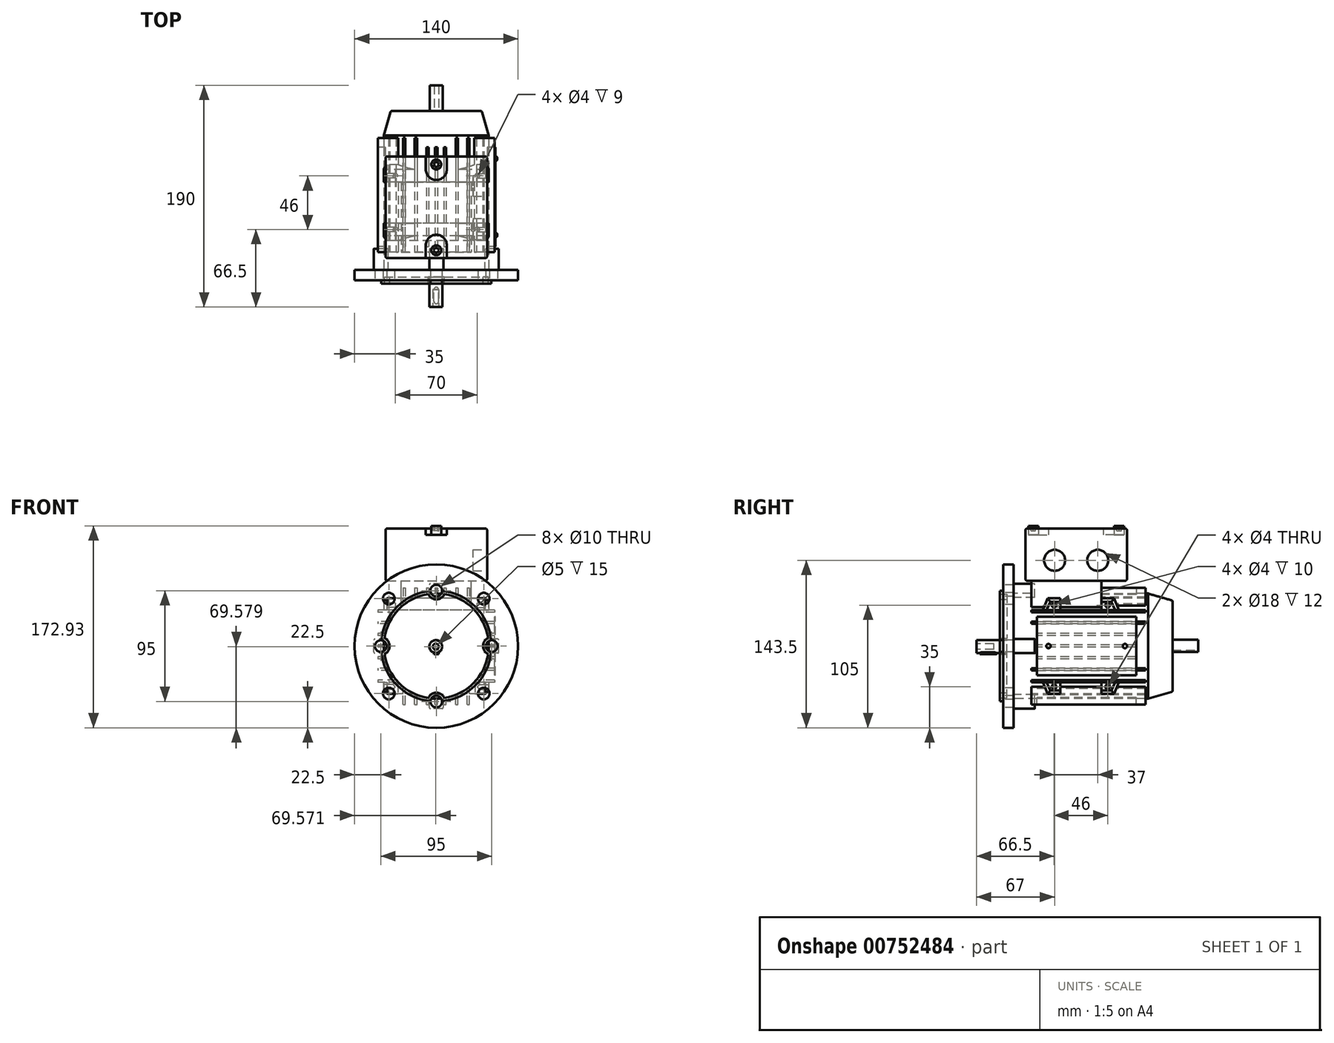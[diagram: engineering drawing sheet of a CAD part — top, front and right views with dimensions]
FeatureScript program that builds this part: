
annotation { "Feature Type Name" : "Feature", "Feature Type Description" : "" }
export const myFeature = defineFeature(function(context is Context, id is Id, definition is map)
    precondition{}
    {
        {
            var Q0;
            Q0=qCreatedBy(makeId("Front.planeOp"),FACE);
            var sketch = newSketch(context, id + "F0", { "sketchPlane" : qUnion([Q0])});
            skCircle(sketch, "E0", {"center": v(0, 0) * mm, "radius": 70 * mm});
            skSolve(sketch);
        }
        {
            var Q0;
            Q0 = qSketchRegion(id + "F0", true);
            extrude(context, id + "F1", {"entities" : qUnion([Q0]), "oppositeDirection" : true, "depth" : 9 * mm, "offsetDistance" : 25.4 * mm});
        }
        {
            var Q0;
            Q0=makeQuery(id+"F1.opExtrude","CAP_FACE",FACE,{"disambiguationData":[OSD([sQuery(id+"F0.wireOp",EDGE,"E0")])],"isStart":true});
            var sketch = newSketch(context, id + "F2", { "sketchPlane" : qUnion([Q0])});
            skCircle(sketch, "E1", {"center": v(-40.66, 40.66) * mm, "radius": 5 * mm});
            skCircle(sketch, "E2", {"center": v(-40.66, -40.66) * mm, "radius": 5 * mm});
            skCircle(sketch, "E3", {"center": v(40.66, -40.66) * mm, "radius": 5 * mm});
            skCircle(sketch, "E4", {"center": v(40.66, 40.66) * mm, "radius": 5 * mm});
            skCircle(sketch, "E5", {"center": v(0, 0) * mm, "radius": 57.5 * mm, "construction": true});
            skLineSegment(sketch, "E6", {"start": v(-40.66, -40.66) * mm, "end": v(40.66, 40.66) * mm, "construction": true});
            skLineSegment(sketch, "E7", {"start": v(-40.66, 40.66) * mm, "end": v(40.66, -40.66) * mm, "construction": true});
            skLineSegment(sketch, "E8", {"start": v(-57.5, 0) * mm, "end": v(57.5, 0) * mm, "construction": true});
            skSolve(sketch);
        }
        {
            var Q0;
            Q0 = qSketchRegion(id + "F2", true);
            extrude(context, id + "F3", {"entities" : qUnion([Q0]), "operationType" : NewBodyOperationType.REMOVE, "endBound" : BoundingType.UP_TO_NEXT, "oppositeDirection" : true, "depth" : 25.4 * mm, "offsetDistance" : 25.4 * mm});
        }
        {
            var Q0;
            Q0=makeQuery(id+"F1.opExtrude","CAP_FACE",FACE,{"disambiguationData":[OSD([sQuery(id+"F0.wireOp",EDGE,"E0")])],"isStart":true});
            var sketch = newSketch(context, id + "F4", { "sketchPlane" : qUnion([Q0])});
            skCircle(sketch, "E9", {"center": v(0, 0) * mm, "radius": 47.5 * mm, "construction": true});
            skCircle(sketch, "E10", {"center": v(0, 47.5) * mm, "radius": 5 * mm});
            skCircle(sketch, "E11", {"center": v(47.5, 0) * mm, "radius": 5 * mm});
            skCircle(sketch, "E12", {"center": v(0, -47.5) * mm, "radius": 5 * mm});
            skCircle(sketch, "E13", {"center": v(-47.5, 0) * mm, "radius": 5 * mm});
            skSolve(sketch);
        }
        {
            var Q0;
            Q0 = qSketchRegion(id + "F4", true);
            extrude(context, id + "F5", {"entities" : qUnion([Q0]), "operationType" : NewBodyOperationType.REMOVE, "endBound" : BoundingType.THROUGH_ALL, "oppositeDirection" : true, "depth" : 8 * mm, "offsetDistance" : 25 * mm});
        }
        {
            var Q0;
            Q0=qCreatedBy(makeId("Front.planeOp"),FACE);
            var sketch = newSketch(context, id + "F6", { "sketchPlane" : qUnion([Q0])});
            skArc(sketch, "E14", {"start": v(-5, 47.24) * mm, "mid": v(-33.59, 33.59) * mm, "end": v(-47.24, 5) * mm});
            skArc(sketch, "E15", {"start": v(-5, 47.24) * mm, "mid": v(0, 42.5) * mm, "end": v(5, 47.24) * mm});
            skArc(sketch, "E16", {"start": v(47.24, 5) * mm, "mid": v(42.5, 0) * mm, "end": v(47.24, -5) * mm});
            skArc(sketch, "E17", {"start": v(5, -47.24) * mm, "mid": v(0, -42.5) * mm, "end": v(-5, -47.24) * mm});
            skArc(sketch, "E18", {"start": v(-47.24, -5) * mm, "mid": v(-42.5, 0) * mm, "end": v(-47.24, 5) * mm});
            skArc(sketch, "E19.trimOffspring", {"start": v(47.24, 5) * mm, "mid": v(33.59, 33.59) * mm, "end": v(5, 47.24) * mm});
            skArc(sketch, "E20.trimOffspring", {"start": v(5, -47.24) * mm, "mid": v(33.59, -33.59) * mm, "end": v(47.24, -5) * mm});
            skArc(sketch, "E21.trimOffspring", {"start": v(-47.24, -5) * mm, "mid": v(-33.59, -33.59) * mm, "end": v(-5, -47.24) * mm});
            skArc(sketch, "E22.0", {"start": v(6.86, -44.47) * mm, "mid": v(31.82, -31.82) * mm, "end": v(44.47, -6.86) * mm});
            skArc(sketch, "E22.1", {"start": v(44.47, 6.86) * mm, "mid": v(40, 0) * mm, "end": v(44.47, -6.86) * mm});
            skArc(sketch, "E22.2", {"start": v(6.86, -44.47) * mm, "mid": v(0, -40) * mm, "end": v(-6.86, -44.47) * mm});
            skArc(sketch, "E22.3", {"start": v(44.47, 6.86) * mm, "mid": v(31.82, 31.82) * mm, "end": v(6.86, 44.47) * mm});
            skArc(sketch, "E22.4", {"start": v(-44.47, -6.86) * mm, "mid": v(-31.82, -31.82) * mm, "end": v(-6.86, -44.47) * mm});
            skArc(sketch, "E22.5", {"start": v(-44.47, -6.86) * mm, "mid": v(-40, 0) * mm, "end": v(-44.47, 6.86) * mm});
            skArc(sketch, "E22.6", {"start": v(-6.86, 44.47) * mm, "mid": v(-31.82, 31.82) * mm, "end": v(-44.47, 6.86) * mm});
            skArc(sketch, "E22.7", {"start": v(-6.86, 44.47) * mm, "mid": v(0, 40) * mm, "end": v(6.86, 44.47) * mm});
            skSolve(sketch);
        }
        {
            var Q0;
            Q0=makeQuery(id+"F6.imprint","IMPRINT",FACE,{"disambiguationData":[TD([[makeQuery(id+"F6.imprint","IMPRINT",EDGE,{"derivedFrom":sQuery(id+"F6.wireOp",EDGE,"E14")}),1.0]])]});
            extrude(context, id + "F7", {"entities" : qUnion([Q0]), "operationType" : NewBodyOperationType.ADD, "depth" : 3 * mm, "offsetDistance" : 25 * mm});
        }
        {
            var Q0;
            Q0=makeQuery(id+"F4.imprint","IMPRINT",FACE,{"disambiguationData":[TD([[makeQuery(id+"F4.imprint","IMPRINT",EDGE,{"derivedFrom":sQuery(id+"F4.wireOp",EDGE,"E10")}),-1.0]])]});
            var sketch = newSketch(context, id + "F8", { "sketchPlane" : qUnion([Q0])});
            skArc(sketch, "E23.0", {"start": v(-6.86, 44.47) * mm, "mid": v(-31.82, 31.82) * mm, "end": v(-44.47, 6.86) * mm});
            skArc(sketch, "E24.0", {"start": v(-6.86, 44.47) * mm, "mid": v(0, 40) * mm, "end": v(6.86, 44.47) * mm});
            skArc(sketch, "E25.0", {"start": v(44.47, 6.86) * mm, "mid": v(31.82, 31.82) * mm, "end": v(6.86, 44.47) * mm});
            skArc(sketch, "E26.0", {"start": v(-44.47, -6.86) * mm, "mid": v(-40, 0) * mm, "end": v(-44.47, 6.86) * mm});
            skArc(sketch, "E27.0", {"start": v(-44.47, -6.86) * mm, "mid": v(-31.82, -31.82) * mm, "end": v(-6.86, -44.47) * mm});
            skArc(sketch, "E28.0", {"start": v(6.86, -44.47) * mm, "mid": v(0, -40) * mm, "end": v(-6.86, -44.47) * mm});
            skArc(sketch, "E29.0", {"start": v(6.86, -44.47) * mm, "mid": v(31.82, -31.82) * mm, "end": v(44.47, -6.86) * mm});
            skArc(sketch, "E30.0", {"start": v(44.47, 6.86) * mm, "mid": v(40, 0) * mm, "end": v(44.47, -6.86) * mm});
            skSolve(sketch);
        }
        {
            var Q0;
            Q0 = qSketchRegion(id + "F8", true);
            extrude(context, id + "F9", {"entities" : qUnion([Q0]), "operationType" : NewBodyOperationType.REMOVE, "oppositeDirection" : true, "depth" : 3 * mm, "offsetDistance" : 25 * mm});
        }
        {
            var Q0;
            Q0=makeQuery(id+"F4.imprint","IMPRINT",FACE,{"disambiguationData":[TD([[makeQuery(id+"F4.imprint","IMPRINT",EDGE,{"derivedFrom":sQuery(id+"F4.wireOp",EDGE,"E10")}),-1.0]])]});
            var sketch = newSketch(context, id + "F10", { "sketchPlane" : qUnion([Q0])});
            skCircle(sketch, "E31", {"center": v(-0.43, -0.42) * mm, "radius": 5.5 * mm});
            skSolve(sketch);
        }
        {
            var Q0;
            Q0 = qSketchRegion(id + "F10", true);
            var Q1;
            Q1=makeQuery(id+"F9.boolean.opBoolean","COPY",FACE,{"derivedFrom":makeQuery(id+"F9.opExtrude","CAP_FACE",FACE,{"disambiguationData":[OSD([sQuery(id+"F8.wireOp",EDGE,"E23.0"),sQuery(id+"F8.wireOp",EDGE,"E24.0"),sQuery(id+"F8.wireOp",EDGE,"E25.0"),sQuery(id+"F8.wireOp",EDGE,"E26.0"),sQuery(id+"F8.wireOp",EDGE,"E27.0"),sQuery(id+"F8.wireOp",EDGE,"E28.0"),sQuery(id+"F8.wireOp",EDGE,"E29.0"),sQuery(id+"F8.wireOp",EDGE,"E30.0")])],"isStart":false})});
            extrude(context, id + "F11", {"entities" : qUnion([Q0]), "depth" : 23 * mm, "offsetDistance" : 25 * mm, "hasSecondDirection" : true, "secondDirectionBound" : SecondDirectionBoundingType.UP_TO_SURFACE, "secondDirectionOppositeDirection" : true, "secondDirectionDepth" : 25 * mm, "secondDirectionBoundEntityFace" : qUnion([Q1])});
        }
        {
            var Q0;
            Q0=qCreatedBy(makeId("Front.planeOp"),FACE);
            cPlane(context, id + "F12", {"entities" : qUnion([Q0]), "cplaneType" : CPlaneType.OFFSET, "offset" : 124 * mm, "oppositeDirection" : true, "width" : 150 * mm, "height" : 150 * mm});
        }
        {
            var Q0;
            Q0=qCreatedBy(id+"F12.planeOp",FACE);
            var sketch = newSketch(context, id + "F13", { "sketchPlane" : qUnion([Q0])});
            skPoint(sketch, "E32.middle", {"position": v(0, 0) * mm});
            skCircle(sketch, "E33", {"center": v(0, 0) * mm, "radius": 56 * mm});
            skSolve(sketch);
        }
        {
            var Q0;
            Q0=makeQuery(id+"F1.opExtrude","CAP_FACE",FACE,{"disambiguationData":[OSD([sQuery(id+"F0.wireOp",EDGE,"E0")])],"isStart":false});
            var sketch = newSketch(context, id + "F14", { "sketchPlane" : qUnion([Q0])});
            skCircle(sketch, "E34", {"center": v(0, 0) * mm, "radius": 45 * mm});
            skSolve(sketch);
        }
        {
            var Q0;
            Q0 = qSketchRegion(id + "F14", true);
            var Q1;
            Q1=makeQuery(id+"Fn6rnlRLXiBt8Ug_1.opExtrude","CAP_FACE",FACE,{"disambiguationData":[OSD([sQuery(id+"F13.wireOp",EDGE,"E33")])],"isStart":true});
            extrude(context, id + "F15", {"entities" : qUnion([Q0]), "depth" : 115 * mm, "endBoundEntityFace" : qUnion([Q1]), "offsetDistance" : 25 * mm});
        }
        {
            var Q0;
            Q0=qCreatedBy(makeId("Right.planeOp"),FACE);
            var sketch = newSketch(context, id + "F16", { "sketchPlane" : qUnion([Q0])});
            skLineSegment(sketch, "E35.bottom", {"start": v(24, 21) * mm, "end": v(122, 21) * mm});
            skLineSegment(sketch, "E35.top", {"start": v(24, 19) * mm, "end": v(122, 19) * mm});
            skLineSegment(sketch, "E35.left", {"start": v(24, 21) * mm, "end": v(24, 19) * mm});
            skLineSegment(sketch, "E35.right", {"start": v(122, 21) * mm, "end": v(122, 19) * mm});
            skLineSegment(sketch, "E36.bottom", {"start": v(29, 11) * mm, "end": v(114, 11) * mm});
            skLineSegment(sketch, "E36.top", {"start": v(29, 9) * mm, "end": v(114, 9) * mm});
            skLineSegment(sketch, "E36.left", {"start": v(29, 11) * mm, "end": v(29, 9) * mm});
            skLineSegment(sketch, "E36.right", {"start": v(114, 11) * mm, "end": v(114, 9) * mm});
            skLineSegment(sketch, "E37.bottom", {"start": v(29, 1) * mm, "end": v(114, 1) * mm});
            skLineSegment(sketch, "E37.top", {"start": v(29, -1) * mm, "end": v(114, -1) * mm});
            skLineSegment(sketch, "E37.left", {"start": v(29, 1) * mm, "end": v(29, -1) * mm});
            skLineSegment(sketch, "E37.right", {"start": v(114, 1) * mm, "end": v(114, -1) * mm});
            skLineSegment(sketch, "E38.bottom", {"start": v(24, 31) * mm, "end": v(122, 31) * mm});
            skLineSegment(sketch, "E38.top", {"start": v(24, 29) * mm, "end": v(122, 29) * mm});
            skLineSegment(sketch, "E38.left", {"start": v(24, 31) * mm, "end": v(24, 29) * mm});
            skLineSegment(sketch, "E38.right", {"start": v(122, 31) * mm, "end": v(122, 29) * mm});
            skLineSegment(sketch, "E39.bottom", {"start": v(29, -9) * mm, "end": v(114, -9) * mm});
            skLineSegment(sketch, "E39.top", {"start": v(29, -11) * mm, "end": v(114, -11) * mm});
            skLineSegment(sketch, "E39.left", {"start": v(29, -9) * mm, "end": v(29, -11) * mm});
            skLineSegment(sketch, "E39.right", {"start": v(114, -9) * mm, "end": v(114, -11) * mm});
            skLineSegment(sketch, "E40.bottom", {"start": v(24, -19) * mm, "end": v(122, -19) * mm});
            skLineSegment(sketch, "E40.top", {"start": v(24, -21) * mm, "end": v(122, -21) * mm});
            skLineSegment(sketch, "E40.left", {"start": v(24, -19) * mm, "end": v(24, -21) * mm});
            skLineSegment(sketch, "E40.right", {"start": v(122, -19) * mm, "end": v(122, -21) * mm});
            skLineSegment(sketch, "E41.bottom", {"start": v(24, -29) * mm, "end": v(122, -29) * mm});
            skLineSegment(sketch, "E41.top", {"start": v(24, -31) * mm, "end": v(122, -31) * mm});
            skLineSegment(sketch, "E41.left", {"start": v(24, -29) * mm, "end": v(24, -31) * mm});
            skLineSegment(sketch, "E41.right", {"start": v(122, -29) * mm, "end": v(122, -31) * mm});
            skLineSegment(sketch, "E42", {"start": v(0, 0) * mm, "end": v(29, 0) * mm, "construction": true});
            skLineSegment(sketch, "E43", {"start": v(122, 29) * mm, "end": v(122, -29) * mm, "construction": true});
            skLineSegment(sketch, "E44", {"start": v(114, 9) * mm, "end": v(114, -9) * mm, "construction": true});
            skSolve(sketch);
        }
        {
            var Q0;
            Q0 = qSketchRegion(id + "F16", true);
            extrude(context, id + "F17", {"entities" : qUnion([Q0]), "operationType" : NewBodyOperationType.ADD, "endBound" : BoundingType.SYMMETRIC, "depth" : 100 * mm, "offsetDistance" : 25 * mm});
        }
        {
            var Q0;
            Q0=qCreatedBy(makeId("Top.planeOp"),FACE);
            cPlane(context, id + "F18", {"entities" : qUnion([Q0]), "cplaneType" : CPlaneType.OFFSET, "offset" : 56 * mm, "width" : 150 * mm, "height" : 150 * mm});
        }
        {
            var Q0;
            Q0=qCreatedBy(id+"F18.planeOp",FACE);
            var sketch = newSketch(context, id + "F19", { "sketchPlane" : qUnion([Q0])});
            skLineSegment(sketch, "E45.bottom", {"start": v(-43.5, 19) * mm, "end": v(43.5, 19) * mm});
            skLineSegment(sketch, "E45.top", {"start": v(-43.5, 106) * mm, "end": v(43.5, 106) * mm});
            skLineSegment(sketch, "E45.left", {"start": v(-43.5, 19) * mm, "end": v(-43.5, 106) * mm});
            skLineSegment(sketch, "E45.right", {"start": v(43.5, 19) * mm, "end": v(43.5, 106) * mm});
            skSolve(sketch);
        }
        {
            var Q0;
            Q0 = qSketchRegion(id + "F19", true);
            extrude(context, id + "F20", {"entities" : qUnion([Q0]), "depth" : 44.68 * mm, "offsetDistance" : 25 * mm});
        }
        {
            var Q0;
            Q0=makeQuery(id+"F1.opExtrude","CAP_FACE",FACE,{"disambiguationData":[OSD([sQuery(id+"F0.wireOp",EDGE,"E0")])],"isStart":false});
            var sketch = newSketch(context, id + "F21", { "sketchPlane" : qUnion([Q0])});
            skLineSegment(sketch, "E46.bottom", {"start": v(41.5, -6) * mm, "end": v(53.5, -6) * mm});
            skLineSegment(sketch, "E46.top", {"start": v(41.5, 6) * mm, "end": v(53.5, 6) * mm});
            skLineSegment(sketch, "E46.left", {"start": v(41.5, -6) * mm, "end": v(41.5, 6) * mm});
            skLineSegment(sketch, "E46.right", {"start": v(53.5, -6) * mm, "end": v(53.5, 6) * mm});
            skPoint(sketch, "E46.middle", {"position": v(47.5, 0) * mm});
            skLineSegment(sketch, "E47.bottom", {"start": v(-6, -53.5) * mm, "end": v(6, -53.5) * mm});
            skLineSegment(sketch, "E47.top", {"start": v(-6, -41.5) * mm, "end": v(6, -41.5) * mm});
            skLineSegment(sketch, "E47.left", {"start": v(-6, -53.5) * mm, "end": v(-6, -41.5) * mm});
            skLineSegment(sketch, "E47.right", {"start": v(6, -53.5) * mm, "end": v(6, -41.5) * mm});
            skPoint(sketch, "E47.middle", {"position": v(0, -47.5) * mm});
            skLineSegment(sketch, "E48.bottom", {"start": v(-53.5, -6) * mm, "end": v(-41.5, -6) * mm});
            skLineSegment(sketch, "E48.top", {"start": v(-53.5, 6) * mm, "end": v(-41.5, 6) * mm});
            skLineSegment(sketch, "E48.left", {"start": v(-53.5, -6) * mm, "end": v(-53.5, 6) * mm});
            skLineSegment(sketch, "E48.right", {"start": v(-41.5, -6) * mm, "end": v(-41.5, 6) * mm});
            skPoint(sketch, "E48.middle", {"position": v(-47.5, 0) * mm});
            skLineSegment(sketch, "E49.bottom", {"start": v(-6, 41.5) * mm, "end": v(6, 41.5) * mm});
            skLineSegment(sketch, "E49.top", {"start": v(-6, 53.5) * mm, "end": v(6, 53.5) * mm});
            skLineSegment(sketch, "E49.left", {"start": v(-6, 41.5) * mm, "end": v(-6, 53.5) * mm});
            skLineSegment(sketch, "E49.right", {"start": v(6, 41.5) * mm, "end": v(6, 53.5) * mm});
            skPoint(sketch, "E49.middle", {"position": v(0, 47.5) * mm});
            skSolve(sketch);
        }
        {
            var Q0;
            Q0 = qSketchRegion(id + "F21", true);
            extrude(context, id + "F22", {"entities" : qUnion([Q0]), "depth" : 18 * mm, "offsetDistance" : 25 * mm});
        }
        {
            var Q0;
            Q0=makeQuery(id+"F20.opExtrude","CAP_FACE",FACE,{"disambiguationData":[OSD([sQuery(id+"F19.wireOp",EDGE,"E45.bottom"),sQuery(id+"F19.wireOp",EDGE,"E45.top"),sQuery(id+"F19.wireOp",EDGE,"E45.left"),sQuery(id+"F19.wireOp",EDGE,"E45.right")])],"isStart":true});
            var sketch = newSketch(context, id + "F23", { "sketchPlane" : qUnion([Q0])});
            skLineSegment(sketch, "E50.bottom", {"start": v(-30, -84) * mm, "end": v(30, -84) * mm});
            skLineSegment(sketch, "E50.top", {"start": v(-30, -24) * mm, "end": v(30, -24) * mm});
            skLineSegment(sketch, "E50.left", {"start": v(-30, -84) * mm, "end": v(-30, -24) * mm});
            skLineSegment(sketch, "E50.right", {"start": v(30, -84) * mm, "end": v(30, -24) * mm});
            skPoint(sketch, "E50.middle", {"position": v(0, -54) * mm});
            skSolve(sketch);
        }
        {
            var Q0;
            Q0 = qSketchRegion(id + "F23", true);
            var Q1;
            Q1=makeQuery(id+"F15.opExtrude","SWEPT_FACE",FACE,{"disambiguationData":[OSD([sQuery(id+"F14.wireOp",EDGE,"E34")])]});
            extrude(context, id + "F24", {"entities" : qUnion([Q0]), "endBound" : BoundingType.UP_TO_SURFACE, "depth" : 25 * mm, "endBoundEntityFace" : qUnion([Q1]), "offsetDistance" : 25 * mm});
        }
        {
            var Q0;
            Q0=qCreatedBy(makeId("Right.planeOp"),FACE);
            var sketch = newSketch(context, id + "F25", { "sketchPlane" : qUnion([Q0])});
            skLineSegment(sketch, "E51.bottom", {"start": v(38.17, -41) * mm, "end": v(49, -41) * mm});
            skLineSegment(sketch, "E51.top", {"start": v(34, -31) * mm, "end": v(49, -31) * mm});
            skLineSegment(sketch, "E51.right", {"start": v(49, -41) * mm, "end": v(49, -31) * mm});
            skLineSegment(sketch, "E52.bottom", {"start": v(84, -41) * mm, "end": v(94.83, -41) * mm});
            skLineSegment(sketch, "E52.top", {"start": v(84, -31) * mm, "end": v(99, -31) * mm});
            skLineSegment(sketch, "E52.left", {"start": v(84, -41) * mm, "end": v(84, -31) * mm});
            skLineSegment(sketch, "E53.bottom", {"start": v(38.17, 41) * mm, "end": v(49, 41) * mm});
            skLineSegment(sketch, "E53.top", {"start": v(34, 31) * mm, "end": v(49, 31) * mm});
            skLineSegment(sketch, "E53.right", {"start": v(49, 41) * mm, "end": v(49, 31) * mm});
            skLineSegment(sketch, "E54.bottom", {"start": v(84, 41) * mm, "end": v(94.83, 41) * mm});
            skLineSegment(sketch, "E54.top", {"start": v(84, 31) * mm, "end": v(99, 31) * mm});
            skLineSegment(sketch, "E54.left", {"start": v(84, 41) * mm, "end": v(84, 31) * mm});
            skLineSegment(sketch, "E55", {"start": v(99, 31) * mm, "end": v(94.83, 41) * mm});
            skLineSegment(sketch, "E56", {"start": v(38.17, -41) * mm, "end": v(34, -31) * mm});
            skLineSegment(sketch, "E57", {"start": v(94.83, -41) * mm, "end": v(99, -31) * mm});
            skLineSegment(sketch, "E58", {"start": v(38.17, 41) * mm, "end": v(34, 31) * mm});
            skLineSegment(sketch, "E59.0", {"start": v(24, 31) * mm, "end": v(122, 31) * mm, "construction": true});
            skLineSegment(sketch, "E60.1", {"start": v(24, -31) * mm, "end": v(122, -31) * mm, "construction": true});
            skLineSegment(sketch, "E61", {"start": v(49, 31) * mm, "end": v(49, -31) * mm, "construction": true});
            skLineSegment(sketch, "E62", {"start": v(84, -31) * mm, "end": v(84, 31) * mm, "construction": true});
            skSolve(sketch);
        }
        {
            var Q0;
            Q0 = qSketchRegion(id + "F25", true);
            extrude(context, id + "F26", {"entities" : qUnion([Q0]), "endBound" : BoundingType.SYMMETRIC, "depth" : 90 * mm, "offsetDistance" : 25 * mm});
        }
        {
            var Q0;
            Q0=makeQuery(id+"F26.opExtrude","CAP_EDGE",EDGE,{"disambiguationData":[OSD([sQuery(id+"F25.wireOp",EDGE,"E51.bottom")])],"isStart":false});
            var Q1;
            Q1=makeQuery(id+"F26.opExtrude","CAP_EDGE",EDGE,{"disambiguationData":[OSD([sQuery(id+"F25.wireOp",EDGE,"E56")])],"isStart":false});
            var Q2;
            Q2=makeQuery(id+"F26.opExtrude","CAP_EDGE",EDGE,{"disambiguationData":[OSD([sQuery(id+"F25.wireOp",EDGE,"E52.bottom")])],"isStart":false});
            var Q3;
            Q3=makeQuery(id+"F26.opExtrude","CAP_EDGE",EDGE,{"disambiguationData":[OSD([sQuery(id+"F25.wireOp",EDGE,"E57")])],"isStart":false});
            var Q4;
            Q4=makeQuery(id+"F26.opExtrude","CAP_EDGE",EDGE,{"disambiguationData":[OSD([sQuery(id+"F25.wireOp",EDGE,"E55")])],"isStart":false});
            var Q5;
            Q5=makeQuery(id+"F26.opExtrude","CAP_EDGE",EDGE,{"disambiguationData":[OSD([sQuery(id+"F25.wireOp",EDGE,"E54.bottom")])],"isStart":false});
            var Q6;
            Q6=makeQuery(id+"F26.opExtrude","CAP_EDGE",EDGE,{"disambiguationData":[OSD([sQuery(id+"F25.wireOp",EDGE,"E53.bottom")])],"isStart":false});
            var Q7;
            Q7=makeQuery(id+"F26.opExtrude","CAP_EDGE",EDGE,{"disambiguationData":[OSD([sQuery(id+"F25.wireOp",EDGE,"E58")])],"isStart":false});
            var Q8;
            Q8=makeQuery(id+"F26.opExtrude","CAP_EDGE",EDGE,{"disambiguationData":[OSD([sQuery(id+"F25.wireOp",EDGE,"E55")])],"isStart":true});
            var Q9;
            Q9=makeQuery(id+"F26.opExtrude","CAP_EDGE",EDGE,{"disambiguationData":[OSD([sQuery(id+"F25.wireOp",EDGE,"E54.bottom")])],"isStart":true});
            var Q10;
            Q10=makeQuery(id+"F26.opExtrude","CAP_EDGE",EDGE,{"disambiguationData":[OSD([sQuery(id+"F25.wireOp",EDGE,"E53.bottom")])],"isStart":true});
            var Q11;
            Q11=makeQuery(id+"F26.opExtrude","CAP_EDGE",EDGE,{"disambiguationData":[OSD([sQuery(id+"F25.wireOp",EDGE,"E58")])],"isStart":true});
            var Q12;
            Q12=makeQuery(id+"F26.opExtrude","CAP_EDGE",EDGE,{"disambiguationData":[OSD([sQuery(id+"F25.wireOp",EDGE,"E57")])],"isStart":true});
            var Q13;
            Q13=makeQuery(id+"F26.opExtrude","CAP_EDGE",EDGE,{"disambiguationData":[OSD([sQuery(id+"F25.wireOp",EDGE,"E52.bottom")])],"isStart":true});
            var Q14;
            Q14=makeQuery(id+"F26.opExtrude","CAP_EDGE",EDGE,{"disambiguationData":[OSD([sQuery(id+"F25.wireOp",EDGE,"E51.bottom")])],"isStart":true});
            var Q15;
            Q15=makeQuery(id+"F26.opExtrude","CAP_EDGE",EDGE,{"disambiguationData":[OSD([sQuery(id+"F25.wireOp",EDGE,"E56")])],"isStart":true});
            chamfer(context, id + "F27", {"entities" : qUnion([Q0, Q1, Q2, Q3, Q4, Q5, Q6, Q7, Q8, Q9, Q10, Q11, Q12, Q13, Q14, Q15]), "width" : 3 * mm, "tangentPropagation" : true});
        }
        {
            var Q0;
            Q0=makeQuery(id+"F26.opExtrude","CAP_FACE",FACE,{"disambiguationData":[OSD([sQuery(id+"F25.wireOp",EDGE,"E54.bottom"),sQuery(id+"F25.wireOp",EDGE,"E54.top"),sQuery(id+"F25.wireOp",EDGE,"E54.left"),sQuery(id+"F25.wireOp",EDGE,"E55")])],"isStart":true});
            var sketch = newSketch(context, id + "F28", { "sketchPlane" : qUnion([Q0])});
            skCircle(sketch, "E63", {"center": v(-89.5, 35) * mm, "radius": 2 * mm});
            skCircle(sketch, "E64", {"center": v(-43.5, 35) * mm, "radius": 2 * mm});
            skCircle(sketch, "E65", {"center": v(-89.5, -35) * mm, "radius": 2 * mm});
            skCircle(sketch, "E66", {"center": v(-43.5, -35) * mm, "radius": 2 * mm});
            skLineSegment(sketch, "E67", {"start": v(-89.5, -35) * mm, "end": v(-84, -35) * mm, "construction": true});
            skLineSegment(sketch, "E68", {"start": v(-89.5, -35) * mm, "end": v(-89.5, -38) * mm, "construction": true});
            skLineSegment(sketch, "E69", {"start": v(-43.5, -35) * mm, "end": v(-49, -35) * mm, "construction": true});
            skLineSegment(sketch, "E70", {"start": v(-89.5, 35) * mm, "end": v(-89.5, 38) * mm, "construction": true});
            skSolve(sketch);
        }
        {
            var Q0;
            Q0 = qSketchRegion(id + "F28", true);
            extrude(context, id + "F29", {"entities" : qUnion([Q0]), "operationType" : NewBodyOperationType.REMOVE, "oppositeDirection" : true, "depth" : 10 * mm, "offsetDistance" : 25 * mm});
        }
        {
            var Q0;
            Q0=makeQuery(id+"F26.opExtrude","CAP_FACE",FACE,{"disambiguationData":[OSD([sQuery(id+"F25.wireOp",EDGE,"E53.bottom"),sQuery(id+"F25.wireOp",EDGE,"E53.top"),sQuery(id+"F25.wireOp",EDGE,"E53.right"),sQuery(id+"F25.wireOp",EDGE,"E58")])],"isStart":false});
            var sketch = newSketch(context, id + "F30", { "sketchPlane" : qUnion([Q0])});
            skCircle(sketch, "E71", {"center": v(43.5, 35) * mm, "radius": 2 * mm});
            skCircle(sketch, "E72", {"center": v(89.5, 35) * mm, "radius": 2 * mm});
            skCircle(sketch, "E73", {"center": v(89.5, -35) * mm, "radius": 2 * mm});
            skCircle(sketch, "E74", {"center": v(43.5, -35) * mm, "radius": 2 * mm});
            skSolve(sketch);
        }
        {
            var Q0;
            Q0 = qSketchRegion(id + "F30", true);
            extrude(context, id + "F31", {"entities" : qUnion([Q0]), "operationType" : NewBodyOperationType.REMOVE, "oppositeDirection" : true, "depth" : 10 * mm, "offsetDistance" : 25 * mm});
        }
        {
            var Q0;
            Q0=makeQuery(id+"F26.opExtrude","SWEPT_FACE",FACE,{"disambiguationData":[OSD([sQuery(id+"F25.wireOp",EDGE,"E52.bottom")])]});
            var sketch = newSketch(context, id + "F32", { "sketchPlane" : qUnion([Q0])});
            skCircle(sketch, "E75", {"center": v(35, -89.5) * mm, "radius": 2 * mm});
            skCircle(sketch, "E76", {"center": v(-35, -89.5) * mm, "radius": 2 * mm});
            skCircle(sketch, "E77", {"center": v(35, -43.5) * mm, "radius": 2 * mm});
            skCircle(sketch, "E78", {"center": v(-35, -43.5) * mm, "radius": 2 * mm});
            skLineSegment(sketch, "E79", {"start": v(35, -89.5) * mm, "end": v(42, -89.5) * mm, "construction": true});
            skLineSegment(sketch, "E80", {"start": v(35, -43.5) * mm, "end": v(35, -49) * mm, "construction": true});
            skLineSegment(sketch, "E81", {"start": v(35, -89.5) * mm, "end": v(35, -84) * mm, "construction": true});
            skLineSegment(sketch, "E82", {"start": v(-35, -89.5) * mm, "end": v(-42, -89.5) * mm, "construction": true});
            skSolve(sketch);
        }
        {
            var Q0;
            Q0 = qSketchRegion(id + "F32", true);
            extrude(context, id + "F33", {"entities" : qUnion([Q0]), "operationType" : NewBodyOperationType.REMOVE, "oppositeDirection" : true, "depth" : 9 * mm, "offsetDistance" : 25 * mm});
        }
        {
            var Q0;
            Q0=makeQuery(id+"F17.opExtrude","CAP_FACE",FACE,{"disambiguationData":[OSD([sQuery(id+"F16.wireOp",EDGE,"E37.bottom"),sQuery(id+"F16.wireOp",EDGE,"E37.top"),sQuery(id+"F16.wireOp",EDGE,"E37.left"),sQuery(id+"F16.wireOp",EDGE,"E37.right")])],"isStart":false});
            var sketch = newSketch(context, id + "F34", { "sketchPlane" : qUnion([Q0])});
            skLineSegment(sketch, "E83.bottom", {"start": v(29, -25) * mm, "end": v(114, -25) * mm});
            skLineSegment(sketch, "E83.top", {"start": v(29, 25) * mm, "end": v(114, 25) * mm});
            skLineSegment(sketch, "E83.left", {"start": v(29, -25) * mm, "end": v(29, 25) * mm});
            skLineSegment(sketch, "E83.right", {"start": v(114, -25) * mm, "end": v(114, 25) * mm});
            skLineSegment(sketch, "E84", {"start": v(71.5, 1) * mm, "end": v(29, 25) * mm, "construction": true});
            skLineSegment(sketch, "E85", {"start": v(71.5, 1) * mm, "end": v(114, 25) * mm, "construction": true});
            skLineSegment(sketch, "E86", {"start": v(71.5, -1) * mm, "end": v(29, -25) * mm, "construction": true});
            skLineSegment(sketch, "E87", {"start": v(71.5, -1) * mm, "end": v(114, -25) * mm, "construction": true});
            skSolve(sketch);
        }
        {
            var Q0;
            Q0 = qSketchRegion(id + "F34", true);
            extrude(context, id + "F35", {"entities" : qUnion([Q0]), "operationType" : NewBodyOperationType.ADD, "depth" : .6 * mm, "offsetDistance" : 25 * mm});
        }
        {
            var Q0;
            Q0=makeQuery(id+"F35.opExtrude","CAP_FACE",FACE,{"disambiguationData":[OSD([sQuery(id+"F34.wireOp",EDGE,"E83.bottom"),sQuery(id+"F34.wireOp",EDGE,"E83.top"),sQuery(id+"F34.wireOp",EDGE,"E83.left"),sQuery(id+"F34.wireOp",EDGE,"E83.right")])],"isStart":false});
            var sketch = newSketch(context, id + "F36", { "sketchPlane" : qUnion([Q0])});
            skCircle(sketch, "E88", {"center": v(38.75, 0) * mm, "radius": 1.88 * mm});
            skCircle(sketch, "E89", {"center": v(104.25, 0) * mm, "radius": 1.88 * mm});
            skLineSegment(sketch, "E90", {"start": v(38.75, 0) * mm, "end": v(29, 0) * mm, "construction": true});
            skLineSegment(sketch, "E91", {"start": v(104.25, 0) * mm, "end": v(114, 0) * mm, "construction": true});
            skSolve(sketch);
        }
        {
            var Q0;
            Q0 = qSketchRegion(id + "F36", true);
            extrude(context, id + "F37", {"entities" : qUnion([Q0]), "operationType" : NewBodyOperationType.ADD, "depth" : 1.5 * mm, "offsetDistance" : 25 * mm});
        }
        {
            var Q0;
            Q0=makeQuery(id+"F37.opExtrude","CAP_EDGE",EDGE,{"disambiguationData":[OSD([sQuery(id+"F36.wireOp",EDGE,"E89")])],"isStart":false});
            var Q1;
            Q1=makeQuery(id+"F37.opExtrude","CAP_EDGE",EDGE,{"disambiguationData":[OSD([sQuery(id+"F36.wireOp",EDGE,"E88")])],"isStart":false});
            fillet(context, id + "F38", {"entities" : qUnion([Q0, Q1]), "radius" : 1 * mm, "tangentPropagation" : true, "allowEdgeOverflow" : false});
        }
        {
            var Q0;
            Q0=makeQuery(id+"F20.opExtrude","CAP_FACE",FACE,{"disambiguationData":[OSD([sQuery(id+"F19.wireOp",EDGE,"E45.bottom"),sQuery(id+"F19.wireOp",EDGE,"E45.top"),sQuery(id+"F19.wireOp",EDGE,"E45.left"),sQuery(id+"F19.wireOp",EDGE,"E45.right")])],"isStart":false});
            var sketch = newSketch(context, id + "F39", { "sketchPlane" : qUnion([Q0])});
            skLineSegment(sketch, "E92", {"start": v(-9, 19) * mm, "end": v(-9, 30) * mm});
            skArc(sketch, "E93", {"start": v(9, 30) * mm, "mid": v(0, 39) * mm, "end": v(-9, 30) * mm});
            skLineSegment(sketch, "E94", {"start": v(9, 30) * mm, "end": v(9, 19) * mm});
            skLineSegment(sketch, "E95", {"start": v(9, 19) * mm, "end": v(-9, 19) * mm});
            skLineSegment(sketch, "E96", {"start": v(0, 30) * mm, "end": v(0, 19) * mm});
            skLineSegment(sketch, "E97", {"start": v(43.5, 62.5) * mm, "end": v(-43.5, 62.5) * mm, "construction": true});
            skArc(sketch, "E98.MirrorCS", {"start": v(9, 95) * mm, "mid": v(0, 86) * mm, "end": v(-9, 95) * mm});
            skLineSegment(sketch, "E99.MirrorCS", {"start": v(9, 95) * mm, "end": v(9, 106) * mm});
            skLineSegment(sketch, "E100.MirrorCS", {"start": v(-9, 106) * mm, "end": v(-9, 95) * mm});
            skLineSegment(sketch, "E101.MirrorCS", {"start": v(9, 106) * mm, "end": v(-9, 106) * mm});
            skSolve(sketch);
        }
        {
            var Q0;
            Q0 = qSketchRegion(id + "F39", true);
            extrude(context, id + "F40", {"entities" : qUnion([Q0]), "operationType" : NewBodyOperationType.REMOVE, "oppositeDirection" : true, "depth" : 5.25 * mm, "offsetDistance" : 25 * mm});
        }
        {
            var Q0;
            Q0=makeQuery(id+"F40.boolean.opBoolean","COPY",FACE,{"derivedFrom":makeQuery(id+"F40.opExtrude","CAP_FACE",FACE,{"disambiguationData":[OSD([sQuery(id+"F39.wireOp",EDGE,"E92"),sQuery(id+"F39.wireOp",EDGE,"E93"),sQuery(id+"F39.wireOp",EDGE,"E94"),sQuery(id+"F39.wireOp",EDGE,"E95")])],"isStart":false})});
            var sketch = newSketch(context, id + "F41", { "sketchPlane" : qUnion([Q0])});
            skCircle(sketch, "E102", {"center": v(0, 25.75) * mm, "radius": 4.25 * mm});
            skPoint(sketch, "E102.centerSnap0", {"position": v(0, 19) * mm});
            skLineSegment(sketch, "E103", {"start": v(0, 19) * mm, "end": v(0, 25.75) * mm, "construction": true});
            skCircle(sketch, "E104.MirrorC", {"center": v(0, 99.25) * mm, "radius": 4.25 * mm});
            skSolve(sketch);
        }
        {
            var Q0;
            Q0 = qSketchRegion(id + "F41", true);
            extrude(context, id + "F42", {"entities" : qUnion([Q0]), "operationType" : NewBodyOperationType.ADD, "depth" : 7.5 * mm, "offsetDistance" : 25 * mm});
        }
        {
            var Q0;
            Q0=makeQuery(id+"F42.opExtrude","CAP_FACE",FACE,{"disambiguationData":[OSD([sQuery(id+"F41.wireOp",EDGE,"E102")])],"isStart":false});
            var sketch = newSketch(context, id + "F43", { "sketchPlane" : qUnion([Q0])});
            skCircle(sketch, "E105.cCircle", {"center": v(0, 25.75) * mm, "radius": 2 * mm, "construction": true});
            skLineSegment(sketch, "E105.0", {"start": v(-1.15, 27.75) * mm, "end": v(1.15, 27.75) * mm});
            skLineSegment(sketch, "E105.1", {"start": v(1.15, 27.75) * mm, "end": v(2.3, 25.75) * mm});
            skLineSegment(sketch, "E105.2", {"start": v(2.3, 25.75) * mm, "end": v(1.15, 23.75) * mm});
            skLineSegment(sketch, "E105.3", {"start": v(1.15, 23.75) * mm, "end": v(-1.15, 23.75) * mm});
            skLineSegment(sketch, "E105.4", {"start": v(-1.15, 23.75) * mm, "end": v(-2.3, 25.75) * mm});
            skLineSegment(sketch, "E105.5", {"start": v(-2.3, 25.75) * mm, "end": v(-1.15, 27.75) * mm});
            skPoint(sketch, "E105.0.midPoint", {"position": v(0, 27.75) * mm});
            skLineSegment(sketch, "E106.MirrorCS", {"start": v(2.3, 99.25) * mm, "end": v(1.15, 101.25) * mm});
            skLineSegment(sketch, "E107.MirrorCS", {"start": v(1.15, 101.25) * mm, "end": v(-1.15, 101.25) * mm});
            skLineSegment(sketch, "E108.MirrorCS", {"start": v(-1.15, 101.25) * mm, "end": v(-2.3, 99.25) * mm});
            skLineSegment(sketch, "E109.MirrorCS", {"start": v(-2.3, 99.25) * mm, "end": v(-1.15, 97.25) * mm});
            skLineSegment(sketch, "E110.MirrorCS", {"start": v(-1.15, 97.25) * mm, "end": v(1.15, 97.25) * mm});
            skLineSegment(sketch, "E111.MirrorCS", {"start": v(1.15, 97.25) * mm, "end": v(2.3, 99.25) * mm});
            skSolve(sketch);
        }
        {
            var Q0;
            Q0 = qSketchRegion(id + "F43", true);
            extrude(context, id + "F44", {"entities" : qUnion([Q0]), "operationType" : NewBodyOperationType.REMOVE, "oppositeDirection" : true, "depth" : 4 * mm, "offsetDistance" : 25 * mm});
        }
        {
            var Q0;
            Q0=makeQuery(id+"F20.opExtrude","CAP_EDGE",EDGE,{"disambiguationData":[OSD([sQuery(id+"F19.wireOp",EDGE,"E45.left")])],"isStart":false});
            var Q1;
            {var subQ0=sQuery(id+"F19.wireOp",EDGE,"E45.bottom");var subQ1=sQuery(id+"F19.wireOp",EDGE,"E45.left");Q1=makeQuery(id+"F40.boolean.opBoolean","SPLIT",EDGE,{"disambiguationData":[TD([makeQuery(id+"F20.opExtrude","SWEPT_FACE",FACE,{"disambiguationData":[OSD([subQ1])]})])],"derivedFrom":makeQuery(id+"F20.opExtrude","CAP_EDGE",EDGE,{"disambiguationData":[OSD([subQ0])],"isStart":false})});}
            var Q2;
            Q2=makeQuery(id+"F40.boolean.opBoolean","COPY",EDGE,{"derivedFrom":makeQuery(id+"F40.opExtrude","CAP_EDGE",EDGE,{"disambiguationData":[OSD([sQuery(id+"F39.wireOp",EDGE,"E92")])],"isStart":true})});
            var Q3;
            Q3=makeQuery(id+"F40.boolean.opBoolean","COPY",EDGE,{"derivedFrom":makeQuery(id+"F40.opExtrude","CAP_EDGE",EDGE,{"disambiguationData":[OSD([sQuery(id+"F39.wireOp",EDGE,"E93")])],"isStart":true})});
            var Q4;
            Q4=makeQuery(id+"F40.boolean.opBoolean","COPY",EDGE,{"derivedFrom":makeQuery(id+"F40.opExtrude","CAP_EDGE",EDGE,{"disambiguationData":[OSD([sQuery(id+"F39.wireOp",EDGE,"E94")])],"isStart":true})});
            var Q5;
            {var subQ0=sQuery(id+"F19.wireOp",EDGE,"E45.bottom");var subQ1=sQuery(id+"F19.wireOp",EDGE,"E45.right");Q5=makeQuery(id+"F40.boolean.opBoolean","SPLIT",EDGE,{"disambiguationData":[TD([makeQuery(id+"F20.opExtrude","SWEPT_FACE",FACE,{"disambiguationData":[OSD([subQ1])]})])],"derivedFrom":makeQuery(id+"F20.opExtrude","CAP_EDGE",EDGE,{"disambiguationData":[OSD([subQ0])],"isStart":false})});}
            var Q6;
            Q6=makeQuery(id+"F20.opExtrude","CAP_EDGE",EDGE,{"disambiguationData":[OSD([sQuery(id+"F19.wireOp",EDGE,"E45.right")])],"isStart":false});
            var Q7;
            {var subQ0=sQuery(id+"F19.wireOp",EDGE,"E45.right");var subQ1=sQuery(id+"F19.wireOp",EDGE,"E45.top");Q7=makeQuery(id+"F40.boolean.opBoolean","SPLIT",EDGE,{"disambiguationData":[TD([makeQuery(id+"F20.opExtrude","SWEPT_FACE",FACE,{"disambiguationData":[OSD([subQ0])]})])],"derivedFrom":makeQuery(id+"F20.opExtrude","CAP_EDGE",EDGE,{"disambiguationData":[OSD([subQ1])],"isStart":false})});}
            var Q8;
            Q8=makeQuery(id+"F40.boolean.opBoolean","COPY",EDGE,{"derivedFrom":makeQuery(id+"F40.opExtrude","CAP_EDGE",EDGE,{"disambiguationData":[OSD([sQuery(id+"F39.wireOp",EDGE,"E99.MirrorCS")])],"isStart":true})});
            var Q9;
            Q9=makeQuery(id+"F40.boolean.opBoolean","COPY",EDGE,{"derivedFrom":makeQuery(id+"F40.opExtrude","CAP_EDGE",EDGE,{"disambiguationData":[OSD([sQuery(id+"F39.wireOp",EDGE,"E98.MirrorCS")])],"isStart":true})});
            var Q10;
            Q10=makeQuery(id+"F40.boolean.opBoolean","COPY",EDGE,{"derivedFrom":makeQuery(id+"F40.opExtrude","CAP_EDGE",EDGE,{"disambiguationData":[OSD([sQuery(id+"F39.wireOp",EDGE,"E100.MirrorCS")])],"isStart":true})});
            var Q11;
            {var subQ0=sQuery(id+"F19.wireOp",EDGE,"E45.left");var subQ1=sQuery(id+"F19.wireOp",EDGE,"E45.top");Q11=makeQuery(id+"F40.boolean.opBoolean","SPLIT",EDGE,{"disambiguationData":[TD([makeQuery(id+"F20.opExtrude","SWEPT_FACE",FACE,{"disambiguationData":[OSD([subQ0])]})])],"derivedFrom":makeQuery(id+"F20.opExtrude","CAP_EDGE",EDGE,{"disambiguationData":[OSD([subQ1])],"isStart":false})});}
            var Q12;
            Q12=makeQuery(id+"F20.opExtrude","SWEPT_EDGE",EDGE,{"disambiguationData":[OSD([sQuery(id+"F19.wireOp",EDGE,"E45.bottom"),sQuery(id+"F19.wireOp",EDGE,"E45.right")])]});
            var Q13;
            Q13=makeQuery(id+"F20.opExtrude","SWEPT_EDGE",EDGE,{"disambiguationData":[OSD([sQuery(id+"F19.wireOp",EDGE,"E45.bottom"),sQuery(id+"F19.wireOp",EDGE,"E45.left")])]});
            var Q14;
            Q14=makeQuery(id+"F20.opExtrude","SWEPT_EDGE",EDGE,{"disambiguationData":[OSD([sQuery(id+"F19.wireOp",EDGE,"E45.top"),sQuery(id+"F19.wireOp",EDGE,"E45.right")])]});
            var Q15;
            Q15=makeQuery(id+"F20.opExtrude","CAP_EDGE",EDGE,{"disambiguationData":[OSD([sQuery(id+"F19.wireOp",EDGE,"E45.left")])],"isStart":true});
            var Q16;
            Q16=makeQuery(id+"F20.opExtrude","SWEPT_EDGE",EDGE,{"disambiguationData":[OSD([sQuery(id+"F19.wireOp",EDGE,"E45.top"),sQuery(id+"F19.wireOp",EDGE,"E45.left")])]});
            var Q17;
            Q17=makeQuery(id+"F20.opExtrude","CAP_EDGE",EDGE,{"disambiguationData":[OSD([sQuery(id+"F19.wireOp",EDGE,"E45.top")])],"isStart":true});
            var Q18;
            Q18=makeQuery(id+"F20.opExtrude","CAP_EDGE",EDGE,{"disambiguationData":[OSD([sQuery(id+"F19.wireOp",EDGE,"E45.right")])],"isStart":true});
            var Q19;
            Q19=makeQuery(id+"F20.opExtrude","CAP_EDGE",EDGE,{"disambiguationData":[OSD([sQuery(id+"F19.wireOp",EDGE,"E45.bottom")])],"isStart":true});
            fillet(context, id + "F45", {"entities" : qUnion([Q0, Q1, Q2, Q3, Q4, Q5, Q6, Q7, Q8, Q9, Q10, Q11, Q12, Q13, Q14, Q15, Q16, Q17, Q18, Q19]), "radius" : 1.5 * mm, "tangentPropagation" : true, "allowEdgeOverflow" : false});
        }
        {
            var Q0;
            Q0=makeQuery(id+"F22.opExtrude","SWEPT_EDGE",EDGE,{"disambiguationData":[OSD([sQuery(id+"F21.wireOp",EDGE,"E48.top"),sQuery(id+"F21.wireOp",EDGE,"E48.left")])]});
            var Q1;
            Q1=makeQuery(id+"F22.opExtrude","SWEPT_EDGE",EDGE,{"disambiguationData":[OSD([sQuery(id+"F21.wireOp",EDGE,"E48.bottom"),sQuery(id+"F21.wireOp",EDGE,"E48.left")])]});
            var Q2;
            Q2=makeQuery(id+"F22.opExtrude","SWEPT_EDGE",EDGE,{"disambiguationData":[OSD([sQuery(id+"F21.wireOp",EDGE,"E47.bottom"),sQuery(id+"F21.wireOp",EDGE,"E47.left")])]});
            var Q3;
            Q3=makeQuery(id+"F22.opExtrude","SWEPT_EDGE",EDGE,{"disambiguationData":[OSD([sQuery(id+"F21.wireOp",EDGE,"E47.bottom"),sQuery(id+"F21.wireOp",EDGE,"E47.right")])]});
            var Q4;
            Q4=makeQuery(id+"F22.opExtrude","SWEPT_EDGE",EDGE,{"disambiguationData":[OSD([sQuery(id+"F21.wireOp",EDGE,"E46.bottom"),sQuery(id+"F21.wireOp",EDGE,"E46.right")])]});
            var Q5;
            Q5=makeQuery(id+"F22.opExtrude","SWEPT_EDGE",EDGE,{"disambiguationData":[OSD([sQuery(id+"F21.wireOp",EDGE,"E46.top"),sQuery(id+"F21.wireOp",EDGE,"E46.right")])]});
            var Q6;
            Q6=makeQuery(id+"F22.opExtrude","SWEPT_EDGE",EDGE,{"disambiguationData":[OSD([sQuery(id+"F21.wireOp",EDGE,"E49.top"),sQuery(id+"F21.wireOp",EDGE,"E49.left")])]});
            var Q7;
            Q7=makeQuery(id+"F22.opExtrude","SWEPT_EDGE",EDGE,{"disambiguationData":[OSD([sQuery(id+"F21.wireOp",EDGE,"E49.top"),sQuery(id+"F21.wireOp",EDGE,"E49.right")])]});
            fillet(context, id + "F46", {"entities" : qUnion([Q0, Q1, Q2, Q3, Q4, Q5, Q6, Q7]), "radius" : 1 * mm, "tangentPropagation" : true, "allowEdgeOverflow" : false});
        }
        {
            var Q0;
            Q0=makeQuery(id+"F20.opExtrude","SWEPT_FACE",FACE,{"disambiguationData":[OSD([sQuery(id+"F19.wireOp",EDGE,"E45.right")])]});
            var sketch = newSketch(context, id + "F47", { "sketchPlane" : qUnion([Q0])});
            skCircle(sketch, "E112", {"center": v(44, 73.5) * mm, "radius": 9 * mm});
            skCircle(sketch, "E113", {"center": v(81, 73.5) * mm, "radius": 9 * mm});
            skLineSegment(sketch, "E114", {"start": v(44, 73.5) * mm, "end": v(19, 73.5) * mm, "construction": true});
            skLineSegment(sketch, "E115", {"start": v(81, 73.5) * mm, "end": v(106, 73.5) * mm, "construction": true});
            skSolve(sketch);
        }
        {
            var Q0;
            Q0 = qSketchRegion(id + "F47", true);
            extrude(context, id + "F48", {"entities" : qUnion([Q0]), "operationType" : NewBodyOperationType.REMOVE, "oppositeDirection" : true, "depth" : 12 * mm, "offsetDistance" : 25 * mm});
        }
        {
            var Q0;
            Q0=makeQuery(id+"F15.opExtrude","CAP_FACE",FACE,{"disambiguationData":[OSD([sQuery(id+"F14.wireOp",EDGE,"E34")])],"isStart":false});
            var sketch = newSketch(context, id + "F49", { "sketchPlane" : qUnion([Q0])});
            skCircle(sketch, "E116", {"center": v(0, 0) * mm, "radius": 45 * mm});
            skSolve(sketch);
        }
        {
            var Q0;
            Q0=makeQuery(id+"F49.imprint","IMPRINT",FACE,{"disambiguationData":[TD([[makeQuery(id+"F49.imprint","IMPRINT",EDGE,{"derivedFrom":sQuery(id+"F49.wireOp",EDGE,"E116")}),1.0]])]});
            cPlane(context, id + "F50", {"entities" : qUnion([Q0]), "cplaneType" : CPlaneType.OFFSET, "offset" : 21 * mm, "width" : 150 * mm, "height" : 150 * mm});
        }
        {
            var Q0;
            Q0=qCreatedBy(id+"F50.planeOp",FACE);
            var sketch = newSketch(context, id + "F51", { "sketchPlane" : qUnion([Q0])});
            skCircle(sketch, "E117", {"center": v(0, 0) * mm, "radius": 39 * mm});
            skSolve(sketch);
        }
        {
            var Q1;
            Q1 = qSketchRegion(id + "F49", true);
            var Q2;
            Q2 = qSketchRegion(id + "F51", true);
            loft(context, id + "F52", {"operationType" : NewBodyOperationType.ADD, "sheetProfilesArray" : [{ "sheetProfileEntities" : qUnion([Q1]) }, { "sheetProfileEntities" : qUnion([Q2]) }]});
        }
        {
            var Q0;
            Q0=makeQuery(id+"F52.opLoft","MID_CAP_EDGE",EDGE,{"disambiguationData":[OSD([sQuery(id+"F51.wireOp",EDGE,"E117")])],"capPos":1.0});
            fillet(context, id + "F53", {"entities" : qUnion([Q0]), "radius" : 1 * mm, "tangentPropagation" : true, "allowEdgeOverflow" : false});
        }
        {
            var Q0;
            Q0=makeQuery(id+"F52.opLoft","CAP_FACE",FACE,{"disambiguationData":[OSD([makeQuery(id+"F51.imprint","IMPRINT",FACE,{"disambiguationData":[TD([[makeQuery(id+"F51.imprint","IMPRINT",EDGE,{"derivedFrom":sQuery(id+"F51.wireOp",EDGE,"E117")}),1.0]])]})])],"isStart":true});
            var sketch = newSketch(context, id + "F54", { "sketchPlane" : qUnion([Q0])});
            skCircle(sketch, "E118", {"center": v(0, 0) * mm, "radius": 5.5 * mm});
            skSolve(sketch);
        }
        {
            var Q0;
            Q0 = qSketchRegion(id + "F54", true);
            extrude(context, id + "F55", {"entities" : qUnion([Q0]), "operationType" : NewBodyOperationType.ADD, "depth" : 22 * mm, "offsetDistance" : 25 * mm});
        }
        {
            var Q0;
            Q0=makeQuery(id+"F55.opExtrude","CAP_FACE",FACE,{"disambiguationData":[OSD([sQuery(id+"F54.wireOp",EDGE,"E118")])],"isStart":false});
            var sketch = newSketch(context, id + "F56", { "sketchPlane" : qUnion([Q0])});
            skLineSegment(sketch, "E119.bottom", {"start": v(-1.9, -3.5) * mm, "end": v(1.9, -3.5) * mm});
            skLineSegment(sketch, "E119.top", {"start": v(-1.9, -5.5) * mm, "end": v(1.9, -5.5) * mm});
            skLineSegment(sketch, "E119.left", {"start": v(-1.9, -3.5) * mm, "end": v(-1.9, -5.5) * mm});
            skLineSegment(sketch, "E119.right", {"start": v(1.9, -3.5) * mm, "end": v(1.9, -5.5) * mm});
            skLineSegment(sketch, "E120", {"start": v(0, 0) * mm, "end": v(0, -3.5) * mm});
            skSolve(sketch);
        }
        {
            var Q0;
            Q0 = qSketchRegion(id + "F56", true);
            var Q1;
            Q1=makeQuery(id+"F52.opLoft","CAP_FACE",FACE,{"disambiguationData":[OSD([makeQuery(id+"F51.imprint","IMPRINT",FACE,{"disambiguationData":[TD([[makeQuery(id+"F51.imprint","IMPRINT",EDGE,{"derivedFrom":sQuery(id+"F51.wireOp",EDGE,"E117")}),1.0]])]})])],"isStart":true});
            extrude(context, id + "F57", {"entities" : qUnion([Q0]), "operationType" : NewBodyOperationType.REMOVE, "endBound" : BoundingType.UP_TO_SURFACE, "oppositeDirection" : true, "depth" : 25 * mm, "endBoundEntityFace" : qUnion([Q1]), "offsetDistance" : 25 * mm});
        }
        {
            var Q0;
            Q0=qCreatedBy(makeId("Top.planeOp"),FACE);
            var sketch = newSketch(context, id + "F58", { "sketchPlane" : qUnion([Q0])});
            skLineSegment(sketch, "E121.bottom", {"start": v(0, -20) * mm, "end": v(0, -20) * mm});
            skLineSegment(sketch, "E121.top", {"start": v(0, -6) * mm, "end": v(0, -6) * mm});
            skLineSegment(sketch, "E121.left", {"start": v(-2, -18) * mm, "end": v(-2, -8) * mm});
            skLineSegment(sketch, "E121.right", {"start": v(2, -18) * mm, "end": v(2, -8) * mm});
            skPoint(sketch, "E121.middle", {"position": v(0, -13) * mm});
            skPoint(sketch, "E122.visualSharp", {"position": v(-2, -20) * mm});
            skArc(sketch, "E122.filletArc", {"start": v(-2, -18) * mm, "mid": v(-1.41, -19.41) * mm, "end": v(0, -20) * mm});
            skPoint(sketch, "E123.visualSharp", {"position": v(2, -20) * mm});
            skArc(sketch, "E123.filletArc", {"start": v(0, -20) * mm, "mid": v(1.41, -19.41) * mm, "end": v(2, -18) * mm});
            skPoint(sketch, "E124.visualSharp", {"position": v(2, -6) * mm});
            skArc(sketch, "E124.filletArc", {"start": v(2, -8) * mm, "mid": v(1.41, -6.59) * mm, "end": v(0, -6) * mm});
            skPoint(sketch, "E125.visualSharp", {"position": v(-2, -6) * mm});
            skArc(sketch, "E125.filletArc", {"start": v(0, -6) * mm, "mid": v(-1.41, -6.59) * mm, "end": v(-2, -8) * mm});
            skSolve(sketch);
        }
        {
            var Q0;
            Q0 = qSketchRegion(id + "F58", true);
            extrude(context, id + "F59", {"entities" : qUnion([Q0]), "operationType" : NewBodyOperationType.ADD, "oppositeDirection" : true, "depth" : 7 * mm, "offsetDistance" : 25 * mm});
        }
        {
            var Q0;
            Q0=makeQuery(id+"F11.opExtrude","CAP_FACE",FACE,{"disambiguationData":[OSD([sQuery(id+"F10.wireOp",EDGE,"E31")])],"isStart":false});
            var sketch = newSketch(context, id + "F60", { "sketchPlane" : qUnion([Q0])});
            skCircle(sketch, "E126", {"center": v(-0.43, -0.42) * mm, "radius": 2.5 * mm});
            skSolve(sketch);
        }
        {
            var Q0;
            Q0 = qSketchRegion(id + "F60", true);
            extrude(context, id + "F61", {"entities" : qUnion([Q0]), "operationType" : NewBodyOperationType.REMOVE, "oppositeDirection" : true, "depth" : 15 * mm, "offsetDistance" : 25 * mm});
        }
        {
            var Q0;
            Q0=qCreatedBy(makeId("Top.planeOp"),FACE);
            var sketch = newSketch(context, id + "F62", { "sketchPlane" : qUnion([Q0])});
            skLineSegment(sketch, "E127.bottom", {"start": v(-18.5, 24) * mm, "end": v(-18.5, 122) * mm});
            skLineSegment(sketch, "E127.top", {"start": v(-16.5, 24) * mm, "end": v(-16.5, 122) * mm});
            skLineSegment(sketch, "E127.left", {"start": v(-18.5, 24) * mm, "end": v(-16.5, 24) * mm});
            skLineSegment(sketch, "E127.right", {"start": v(-18.5, 122) * mm, "end": v(-16.5, 122) * mm});
            skLineSegment(sketch, "E128.bottom", {"start": v(-8.5, 29) * mm, "end": v(-8.5, 114) * mm});
            skLineSegment(sketch, "E128.top", {"start": v(-6.5, 29) * mm, "end": v(-6.5, 114) * mm});
            skLineSegment(sketch, "E128.left", {"start": v(-8.5, 29) * mm, "end": v(-6.5, 29) * mm});
            skLineSegment(sketch, "E128.right", {"start": v(-8.5, 114) * mm, "end": v(-6.5, 114) * mm});
            skLineSegment(sketch, "E129.bottom", {"start": v(-1, 29) * mm, "end": v(-1, 114) * mm});
            skLineSegment(sketch, "E129.top", {"start": v(1, 29) * mm, "end": v(1, 114) * mm});
            skLineSegment(sketch, "E129.left", {"start": v(-1, 29) * mm, "end": v(1, 29) * mm});
            skLineSegment(sketch, "E129.right", {"start": v(-1, 114) * mm, "end": v(1, 114) * mm});
            skLineSegment(sketch, "E130.bottom", {"start": v(-28.5, 24) * mm, "end": v(-28.5, 122) * mm});
            skLineSegment(sketch, "E130.top", {"start": v(-26.5, 24) * mm, "end": v(-26.5, 122) * mm});
            skLineSegment(sketch, "E130.left", {"start": v(-28.5, 24) * mm, "end": v(-26.5, 24) * mm});
            skLineSegment(sketch, "E130.right", {"start": v(-28.5, 122) * mm, "end": v(-26.5, 122) * mm});
            skLineSegment(sketch, "E131.bottom", {"start": v(6.5, 29) * mm, "end": v(6.5, 114) * mm});
            skLineSegment(sketch, "E131.top", {"start": v(8.5, 29) * mm, "end": v(8.5, 114) * mm});
            skLineSegment(sketch, "E131.left", {"start": v(6.5, 29) * mm, "end": v(8.5, 29) * mm});
            skLineSegment(sketch, "E131.right", {"start": v(6.5, 114) * mm, "end": v(8.5, 114) * mm});
            skLineSegment(sketch, "E132.bottom", {"start": v(16.5, 24) * mm, "end": v(16.5, 122) * mm});
            skLineSegment(sketch, "E132.top", {"start": v(18.5, 24) * mm, "end": v(18.5, 122) * mm});
            skLineSegment(sketch, "E132.left", {"start": v(16.5, 24) * mm, "end": v(18.5, 24) * mm});
            skLineSegment(sketch, "E132.right", {"start": v(16.5, 122) * mm, "end": v(18.5, 122) * mm});
            skLineSegment(sketch, "E133.bottom", {"start": v(26.5, 24) * mm, "end": v(26.5, 122) * mm});
            skLineSegment(sketch, "E133.top", {"start": v(28.5, 24) * mm, "end": v(28.5, 122) * mm});
            skLineSegment(sketch, "E133.left", {"start": v(26.5, 24) * mm, "end": v(28.5, 24) * mm});
            skLineSegment(sketch, "E133.right", {"start": v(26.5, 122) * mm, "end": v(28.5, 122) * mm});
            skLineSegment(sketch, "E134", {"start": v(0, -55) * mm, "end": v(0, -26) * mm, "construction": true});
            skLineSegment(sketch, "E135", {"start": v(-26.5, 122) * mm, "end": v(26.5, 122) * mm, "construction": true});
            skLineSegment(sketch, "E136", {"start": v(-6.5, 114) * mm, "end": v(6.5, 114) * mm, "construction": true});
            skLineSegment(sketch, "E137", {"start": v(0, 114) * mm, "end": v(0, 118.89) * mm, "construction": true});
            skSolve(sketch);
        }
        {
            var Q0;
            Q0 = qSketchRegion(id + "F62", true);
            extrude(context, id + "F63", {"entities" : qUnion([Q0]), "operationType" : NewBodyOperationType.ADD, "oppositeDirection" : true, "depth" : 50 * mm, "offsetDistance" : 25 * mm});
        }
        {
            var Q0;
            Q0=qCreatedBy(makeId("Top.planeOp"),FACE);
            var sketch = newSketch(context, id + "F64", { "sketchPlane" : qUnion([Q0])});
            skLineSegment(sketch, "E138.0", {"start": v(-28.5, 24) * mm, "end": v(-28.5, 122) * mm, "construction": true});
            skLineSegment(sketch, "E139.0", {"start": v(-26.5, 24) * mm, "end": v(-26.5, 122) * mm, "construction": true});
            skLineSegment(sketch, "E140.0", {"start": v(-28.5, 122) * mm, "end": v(-26.5, 122) * mm});
            skLineSegment(sketch, "E141.0", {"start": v(-16.5, 24) * mm, "end": v(-16.5, 122) * mm, "construction": true});
            skLineSegment(sketch, "E142.0", {"start": v(-18.5, 24) * mm, "end": v(-18.5, 122) * mm, "construction": true});
            skLineSegment(sketch, "E143.0", {"start": v(-18.5, 122) * mm, "end": v(-16.5, 122) * mm, "construction": true});
            skLineSegment(sketch, "E144.0", {"start": v(-6.5, 29) * mm, "end": v(-6.5, 114) * mm, "construction": true});
            skLineSegment(sketch, "E145.0", {"start": v(-8.5, 29) * mm, "end": v(-8.5, 114) * mm, "construction": true});
            skLineSegment(sketch, "E146.0", {"start": v(-8.5, 114) * mm, "end": v(-6.5, 114) * mm, "construction": true});
            skLineSegment(sketch, "E147.0", {"start": v(1, 29) * mm, "end": v(1, 114) * mm, "construction": true});
            skLineSegment(sketch, "E148.0", {"start": v(-1, 114) * mm, "end": v(1, 114) * mm, "construction": true});
            skLineSegment(sketch, "E149.0", {"start": v(-1, 29) * mm, "end": v(-1, 114) * mm, "construction": true});
            skLineSegment(sketch, "E150.0", {"start": v(6.5, 29) * mm, "end": v(6.5, 114) * mm, "construction": true});
            skLineSegment(sketch, "E151.0", {"start": v(6.5, 114) * mm, "end": v(8.5, 114) * mm, "construction": true});
            skLineSegment(sketch, "E152.0", {"start": v(8.5, 29) * mm, "end": v(8.5, 114) * mm, "construction": true});
            skLineSegment(sketch, "E153.0", {"start": v(16.5, 24) * mm, "end": v(16.5, 122) * mm, "construction": true});
            skLineSegment(sketch, "E154.0", {"start": v(16.5, 122) * mm, "end": v(18.5, 122) * mm, "construction": true});
            skLineSegment(sketch, "E155.0", {"start": v(18.5, 24) * mm, "end": v(18.5, 122) * mm, "construction": true});
            skLineSegment(sketch, "E156.0", {"start": v(26.5, 24) * mm, "end": v(26.5, 122) * mm, "construction": true});
            skLineSegment(sketch, "E157.0", {"start": v(26.5, 122) * mm, "end": v(28.5, 122) * mm, "construction": true});
            skLineSegment(sketch, "E158.0", {"start": v(28.5, 24) * mm, "end": v(28.5, 122) * mm, "construction": true});
            skLineSegment(sketch, "E159.top", {"start": v(-28.5, 84) * mm, "end": v(-26.5, 84) * mm});
            skLineSegment(sketch, "E159.left", {"start": v(-28.5, 122) * mm, "end": v(-28.5, 84) * mm});
            skLineSegment(sketch, "E159.right", {"start": v(-26.5, 122) * mm, "end": v(-26.5, 84) * mm});
            skLineSegment(sketch, "E160.bottom", {"start": v(-18.5, 122) * mm, "end": v(-16.5, 122) * mm});
            skLineSegment(sketch, "E160.top", {"start": v(-18.5, 84) * mm, "end": v(-16.5, 84) * mm});
            skLineSegment(sketch, "E160.left", {"start": v(-18.5, 122) * mm, "end": v(-18.5, 84) * mm});
            skLineSegment(sketch, "E160.right", {"start": v(-16.5, 122) * mm, "end": v(-16.5, 84) * mm});
            skLineSegment(sketch, "E161.bottom", {"start": v(-8.5, 114) * mm, "end": v(-6.5, 114) * mm});
            skLineSegment(sketch, "E161.top", {"start": v(-8.5, 84) * mm, "end": v(-6.5, 84) * mm});
            skLineSegment(sketch, "E161.left", {"start": v(-8.5, 114) * mm, "end": v(-8.5, 84) * mm});
            skLineSegment(sketch, "E161.right", {"start": v(-6.5, 114) * mm, "end": v(-6.5, 84) * mm});
            skLineSegment(sketch, "E162.bottom", {"start": v(-1, 114) * mm, "end": v(1, 114) * mm});
            skLineSegment(sketch, "E162.top", {"start": v(-1, 84) * mm, "end": v(1, 84) * mm});
            skLineSegment(sketch, "E162.left", {"start": v(-1, 114) * mm, "end": v(-1, 84) * mm});
            skLineSegment(sketch, "E162.right", {"start": v(1, 114) * mm, "end": v(1, 84) * mm});
            skLineSegment(sketch, "E163.bottom", {"start": v(6.5, 114) * mm, "end": v(8.5, 114) * mm});
            skLineSegment(sketch, "E163.top", {"start": v(6.5, 84) * mm, "end": v(8.5, 84) * mm});
            skLineSegment(sketch, "E163.left", {"start": v(6.5, 114) * mm, "end": v(6.5, 84) * mm});
            skLineSegment(sketch, "E163.right", {"start": v(8.5, 114) * mm, "end": v(8.5, 84) * mm});
            skLineSegment(sketch, "E164.bottom", {"start": v(16.5, 122) * mm, "end": v(18.5, 122) * mm});
            skLineSegment(sketch, "E164.top", {"start": v(16.5, 84) * mm, "end": v(18.5, 84) * mm});
            skLineSegment(sketch, "E164.left", {"start": v(16.5, 122) * mm, "end": v(16.5, 84) * mm});
            skLineSegment(sketch, "E164.right", {"start": v(18.5, 122) * mm, "end": v(18.5, 84) * mm});
            skLineSegment(sketch, "E165.bottom", {"start": v(26.5, 122) * mm, "end": v(28.5, 122) * mm});
            skLineSegment(sketch, "E165.top", {"start": v(26.5, 84) * mm, "end": v(28.5, 84) * mm});
            skLineSegment(sketch, "E165.left", {"start": v(26.5, 122) * mm, "end": v(26.5, 84) * mm});
            skLineSegment(sketch, "E165.right", {"start": v(28.5, 122) * mm, "end": v(28.5, 84) * mm});
            skSolve(sketch);
        }
        {
            var Q0;
            Q0 = qSketchRegion(id + "F64", true);
            extrude(context, id + "F65", {"entities" : qUnion([Q0]), "operationType" : NewBodyOperationType.ADD, "depth" : 50 * mm, "offsetDistance" : 25 * mm});
        }
    });
